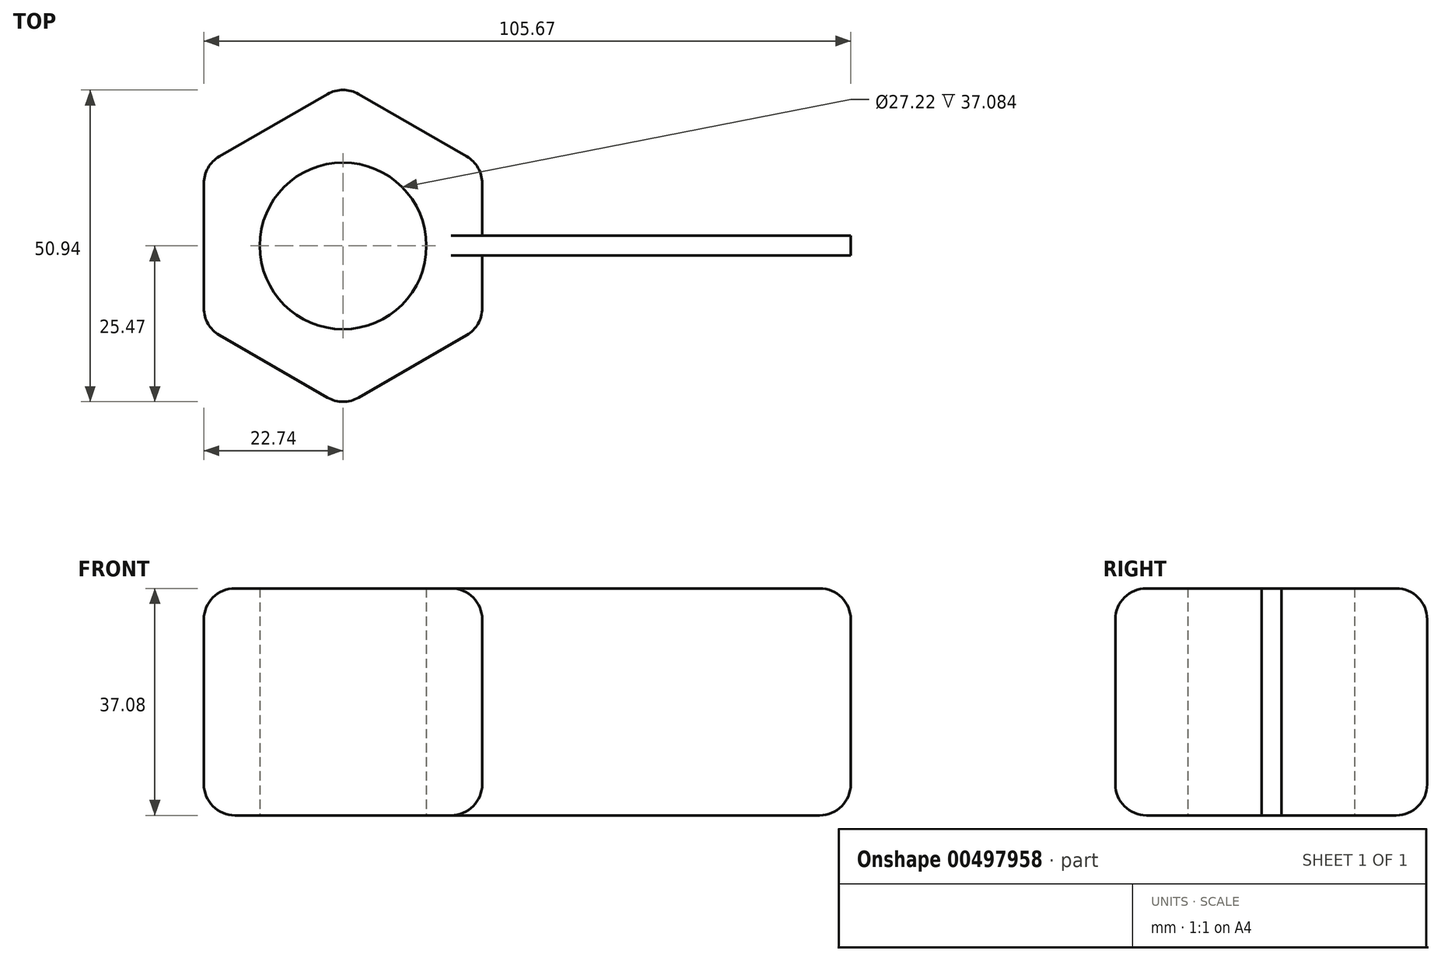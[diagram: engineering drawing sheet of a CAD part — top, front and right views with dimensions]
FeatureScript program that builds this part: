
annotation { "Feature Type Name" : "Feature", "Feature Type Description" : "" }
export const myFeature = defineFeature(function(context is Context, id is Id, definition is map)
    precondition{}
    {
        {
            var Q0;
            Q0=qCreatedBy(makeId("Top.planeOp"),FACE);
            var sketch = newSketch(context, id + "F0", { "sketchPlane" : qUnion([Q0])});
            skCircle(sketch, "E0", {"center": v(0, 0) * mm, "radius": 13.61 * mm});
            skCircle(sketch, "E1.cCircle", {"center": v(0, 0) * mm, "radius": 22.74 * mm, "construction": true});
            skLineSegment(sketch, "E1.0", {"start": v(22.74, 13.13) * mm, "end": v(22.74, -13.13) * mm});
            skLineSegment(sketch, "E1.1", {"start": v(22.74, -13.13) * mm, "end": v(0, -26.25) * mm});
            skLineSegment(sketch, "E1.2", {"start": v(0, -26.25) * mm, "end": v(-22.74, -13.13) * mm});
            skLineSegment(sketch, "E1.3", {"start": v(-22.74, -13.13) * mm, "end": v(-22.74, 13.13) * mm});
            skLineSegment(sketch, "E1.4", {"start": v(-22.74, 13.13) * mm, "end": v(0, 26.25) * mm});
            skLineSegment(sketch, "E1.5", {"start": v(0, 26.25) * mm, "end": v(22.74, 13.13) * mm});
            skPoint(sketch, "E1.0.midPoint", {"position": v(22.74, 0) * mm});
            skSolve(sketch);
        }
        {
            var Q0;
            Q0=makeQuery(id+"F0.imprint","IMPRINT",FACE,{"disambiguationData":[TD([[makeQuery(id+"F0.imprint","IMPRINT",EDGE,{"derivedFrom":sQuery(id+"F0.wireOp",EDGE,"E0")}),-1.0]])]});
            extrude(context, id + "F1", {"entities" : qUnion([Q0]), "depth" : 37.08 * mm});
        }
        {
            var Q0;
            Q0=makeQuery(id+"F1.opExtrude","SWEPT_FACE",FACE,{"disambiguationData":[OSD([sQuery(id+"F0.wireOp",EDGE,"E1.0")])]});
            var sketch = newSketch(context, id + "F2", { "sketchPlane" : qUnion([Q0])});
            skLineSegment(sketch, "E2.bottom", {"start": v(-1.54, 37.08) * mm, "end": v(1.67, 37.08) * mm});
            skLineSegment(sketch, "E2.top", {"start": v(-1.54, 0) * mm, "end": v(1.67, 0) * mm});
            skLineSegment(sketch, "E2.left", {"start": v(-1.54, 37.08) * mm, "end": v(-1.54, 0) * mm});
            skLineSegment(sketch, "E2.right", {"start": v(1.67, 37.08) * mm, "end": v(1.67, 0) * mm});
            skSolve(sketch);
        }
        {
            var Q0;
            Q0=makeQuery(id+"F2.imprint","IMPRINT",FACE,{"disambiguationData":[TD([[makeQuery(id+"F2.imprint","IMPRINT",EDGE,{"derivedFrom":sQuery(id+"F2.wireOp",EDGE,"E2.bottom")}),1.0]])]});
            extrude(context, id + "F3", {"entities" : qUnion([Q0]), "operationType" : NewBodyOperationType.ADD, "depth" : 60.2 * mm});
        }
        {
            var Q0;
            Q0=makeQuery(id+"F1.opExtrude","CAP_EDGE",EDGE,{"disambiguationData":[OSD([sQuery(id+"F0.wireOp",EDGE,"E1.2")])],"isStart":false});
            var Q1;
            {var subQ0=sQuery(id+"F0.wireOp",EDGE,"E1.5");var subQ1=sQuery(id+"F0.wireOp",EDGE,"E1.0");Q1=makeQuery(id+"F3.boolean.opBoolean","SPLIT",EDGE,{"disambiguationData":[TD([makeQuery(id+"F1.opExtrude","SWEPT_FACE",FACE,{"disambiguationData":[OSD([subQ0])]})])],"derivedFrom":makeQuery(id+"F1.opExtrude","CAP_EDGE",EDGE,{"disambiguationData":[OSD([subQ1])],"isStart":false})});}
            var Q2;
            {var subQ0=sQuery(id+"F0.wireOp",EDGE,"E1.1");var subQ1=sQuery(id+"F0.wireOp",EDGE,"E1.0");Q2=makeQuery(id+"F3.boolean.opBoolean","SPLIT",EDGE,{"disambiguationData":[TD([makeQuery(id+"F1.opExtrude","SWEPT_FACE",FACE,{"disambiguationData":[OSD([subQ0])]})])],"derivedFrom":makeQuery(id+"F1.opExtrude","CAP_EDGE",EDGE,{"disambiguationData":[OSD([subQ1])],"isStart":false})});}
            var Q3;
            Q3=makeQuery(id+"F1.opExtrude","CAP_EDGE",EDGE,{"disambiguationData":[OSD([sQuery(id+"F0.wireOp",EDGE,"E1.5")])],"isStart":false});
            var Q4;
            Q4=makeQuery(id+"F1.opExtrude","CAP_EDGE",EDGE,{"disambiguationData":[OSD([sQuery(id+"F0.wireOp",EDGE,"E1.4")])],"isStart":false});
            var Q5;
            Q5=makeQuery(id+"F1.opExtrude","CAP_EDGE",EDGE,{"disambiguationData":[OSD([sQuery(id+"F0.wireOp",EDGE,"E1.3")])],"isStart":false});
            var Q6;
            Q6=makeQuery(id+"F1.opExtrude","CAP_EDGE",EDGE,{"disambiguationData":[OSD([sQuery(id+"F0.wireOp",EDGE,"E1.5")])],"isStart":true});
            var Q7;
            Q7=makeQuery(id+"F1.opExtrude","CAP_EDGE",EDGE,{"disambiguationData":[OSD([sQuery(id+"F0.wireOp",EDGE,"E1.4")])],"isStart":true});
            var Q8;
            Q8=makeQuery(id+"F1.opExtrude","CAP_EDGE",EDGE,{"disambiguationData":[OSD([sQuery(id+"F0.wireOp",EDGE,"E1.3")])],"isStart":true});
            var Q9;
            Q9=makeQuery(id+"F1.opExtrude","CAP_EDGE",EDGE,{"disambiguationData":[OSD([sQuery(id+"F0.wireOp",EDGE,"E1.2")])],"isStart":true});
            var Q10;
            Q10=makeQuery(id+"F1.opExtrude","CAP_EDGE",EDGE,{"disambiguationData":[OSD([sQuery(id+"F0.wireOp",EDGE,"E1.1")])],"isStart":true});
            var Q11;
            {var subQ0=sQuery(id+"F0.wireOp",EDGE,"E1.1");var subQ1=sQuery(id+"F0.wireOp",EDGE,"E1.0");Q11=makeQuery(id+"F3.boolean.opBoolean","SPLIT",EDGE,{"disambiguationData":[TD([makeQuery(id+"F1.opExtrude","SWEPT_FACE",FACE,{"disambiguationData":[OSD([subQ0])]})])],"derivedFrom":makeQuery(id+"F1.opExtrude","CAP_EDGE",EDGE,{"disambiguationData":[OSD([subQ1])],"isStart":true})});}
            var Q12;
            {var subQ0=sQuery(id+"F0.wireOp",EDGE,"E1.5");var subQ1=sQuery(id+"F0.wireOp",EDGE,"E1.0");Q12=makeQuery(id+"F3.boolean.opBoolean","SPLIT",EDGE,{"disambiguationData":[TD([makeQuery(id+"F1.opExtrude","SWEPT_FACE",FACE,{"disambiguationData":[OSD([subQ0])]})])],"derivedFrom":makeQuery(id+"F1.opExtrude","CAP_EDGE",EDGE,{"disambiguationData":[OSD([subQ1])],"isStart":true})});}
            var Q13;
            Q13=makeQuery(id+"F3.opExtrude","CAP_EDGE",EDGE,{"disambiguationData":[OSD([sQuery(id+"F2.wireOp",EDGE,"E2.top")])],"isStart":false});
            var Q14;
            Q14=makeQuery(id+"F3.opExtrude","CAP_EDGE",EDGE,{"disambiguationData":[OSD([sQuery(id+"F2.wireOp",EDGE,"E2.bottom")])],"isStart":false});
            var Q15;
            Q15=makeQuery(id+"F1.opExtrude","CAP_EDGE",EDGE,{"disambiguationData":[OSD([sQuery(id+"F0.wireOp",EDGE,"E1.1")])],"isStart":false});
            var Q16;
            Q16=makeQuery(id+"F1.opExtrude","SWEPT_EDGE",EDGE,{"disambiguationData":[OSD([sQuery(id+"F0.wireOp",EDGE,"E1.3"),sQuery(id+"F0.wireOp",EDGE,"E1.4")])]});
            var Q17;
            Q17=makeQuery(id+"F1.opExtrude","SWEPT_FACE",FACE,{"disambiguationData":[OSD([sQuery(id+"F0.wireOp",EDGE,"E1.5")])]});
            var Q18;
            Q18=makeQuery(id+"F1.opExtrude","SWEPT_FACE",FACE,{"disambiguationData":[OSD([sQuery(id+"F0.wireOp",EDGE,"E1.3")])]});
            var Q19;
            Q19=makeQuery(id+"F1.opExtrude","SWEPT_EDGE",EDGE,{"disambiguationData":[OSD([sQuery(id+"F0.wireOp",EDGE,"E1.1"),sQuery(id+"F0.wireOp",EDGE,"E1.2")])]});
            var Q20;
            Q20=makeQuery(id+"F1.opExtrude","SWEPT_FACE",FACE,{"disambiguationData":[OSD([sQuery(id+"F0.wireOp",EDGE,"E1.1")])]});
            fillet(context, id + "F4", {"entities" : qUnion([Q0, Q1, Q2, Q3, Q4, Q5, Q6, Q7, Q8, Q9, Q10, Q11, Q12, Q13, Q14, Q15, Q16, Q17, Q18, Q19, Q20]), "radius" : 5.08 * mm, "tangentPropagation" : true, "allowEdgeOverflow" : false});
        }
    });
